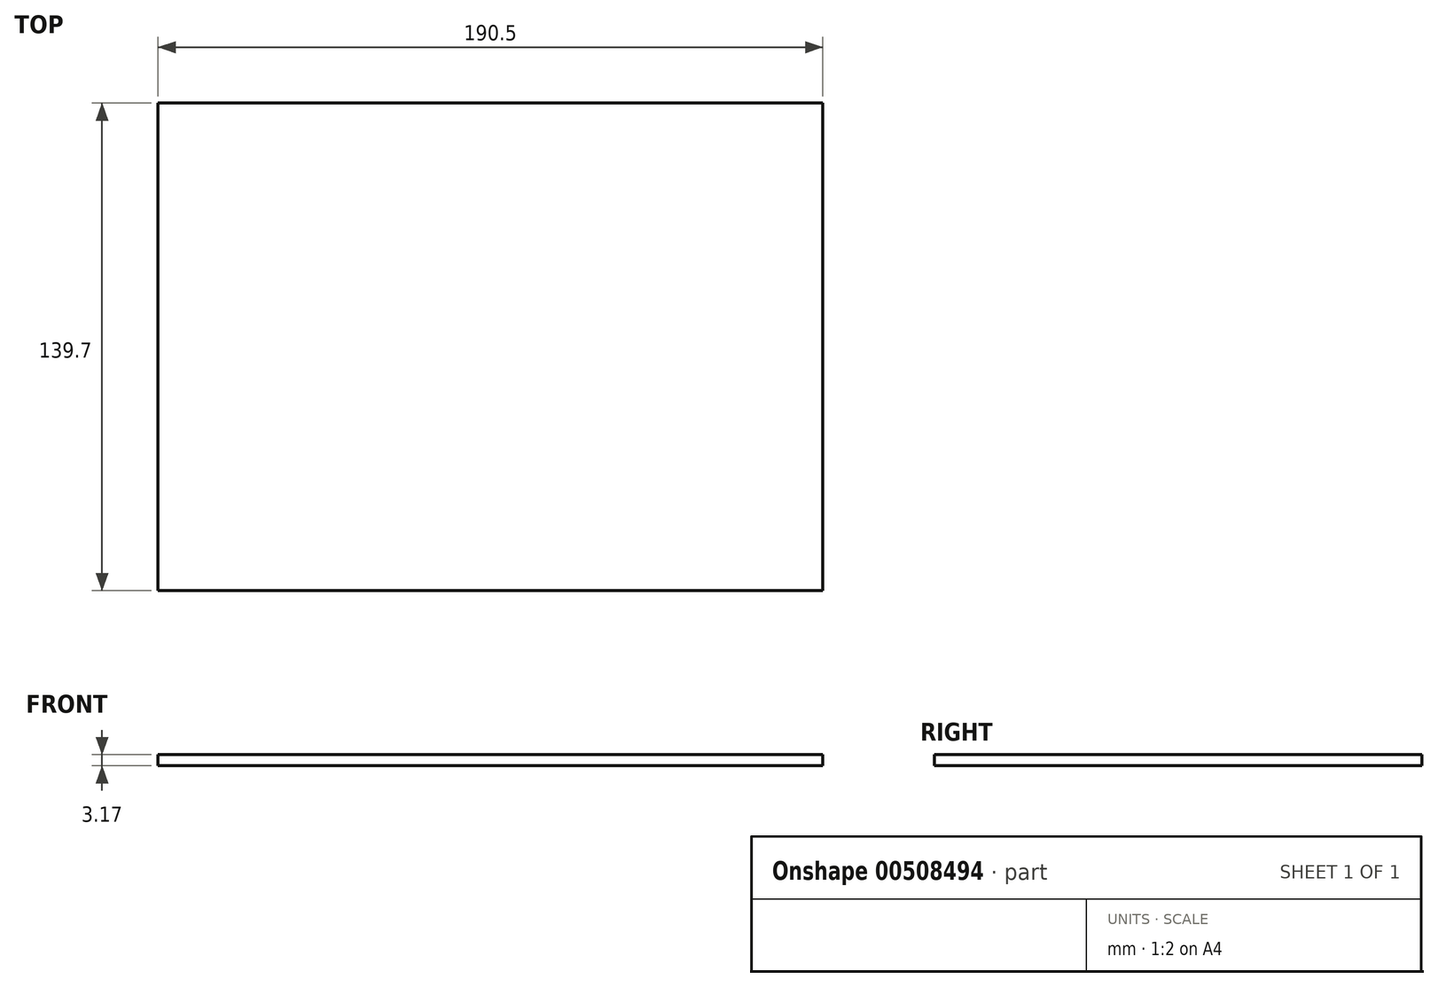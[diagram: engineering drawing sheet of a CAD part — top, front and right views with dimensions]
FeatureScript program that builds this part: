
annotation { "Feature Type Name" : "Feature", "Feature Type Description" : "" }
export const myFeature = defineFeature(function(context is Context, id is Id, definition is map)
    precondition{}
    {
        {
            var Q0;
            Q0=qCreatedBy(makeId("Top.planeOp"),FACE);
            var sketch = newSketch(context, id + "F0", { "sketchPlane" : qUnion([Q0])});
            skLineSegment(sketch, "E0.bottom", {"start": v(95.25, -69.85) * mm, "end": v(-95.25, -69.85) * mm});
            skLineSegment(sketch, "E0.top", {"start": v(95.25, 69.85) * mm, "end": v(-95.25, 69.85) * mm});
            skLineSegment(sketch, "E0.left", {"start": v(95.25, -69.85) * mm, "end": v(95.25, 69.85) * mm});
            skLineSegment(sketch, "E0.right", {"start": v(-95.25, -69.85) * mm, "end": v(-95.25, 69.85) * mm});
            skPoint(sketch, "E0.middle", {"position": v(0, 0) * mm});
            skSolve(sketch);
        }
        {
            var Q0;
            Q0 = qSketchRegion(id + "F0", true);
            extrude(context, id + "F1", {"entities" : qUnion([Q0]), "depth" : 3.17 * mm, "offsetDistance" : 25.4 * mm});
        }
    });
